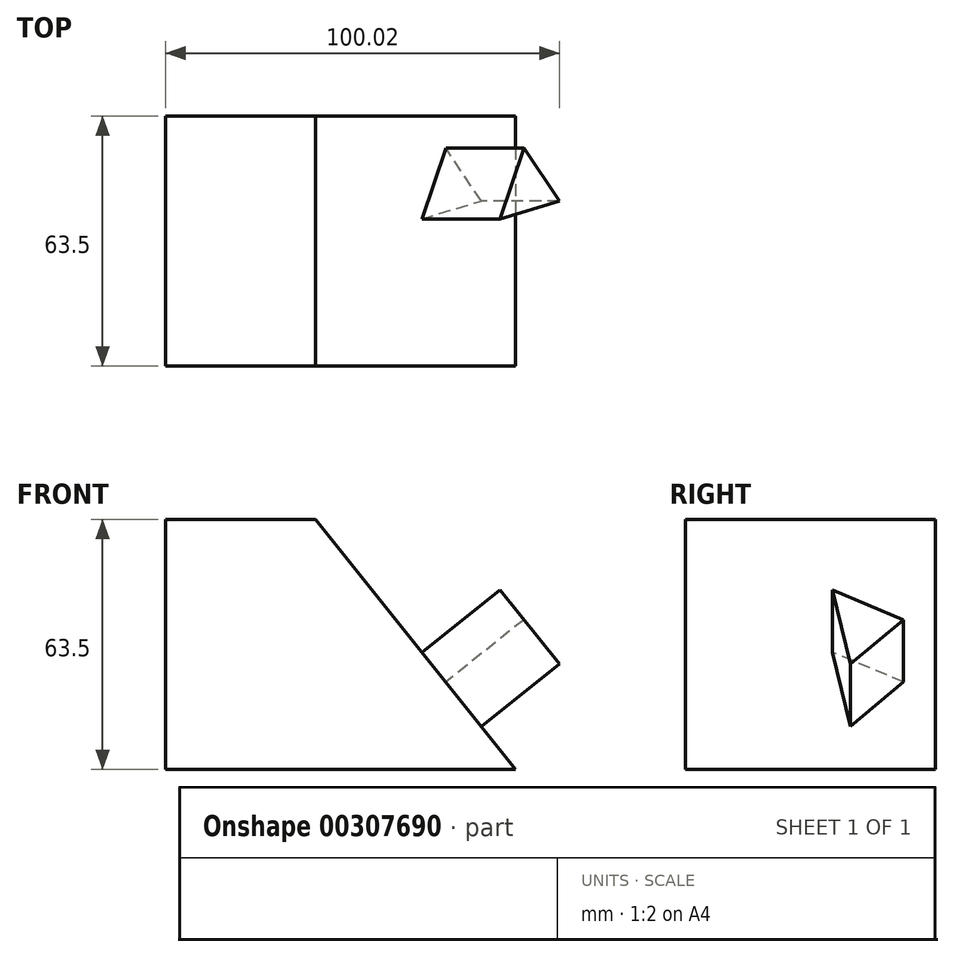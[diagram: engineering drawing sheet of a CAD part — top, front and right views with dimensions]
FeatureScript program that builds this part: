
annotation { "Feature Type Name" : "Feature", "Feature Type Description" : "" }
export const myFeature = defineFeature(function(context is Context, id is Id, definition is map)
    precondition{}
    {
        {
            var Q0;
            Q0=qCreatedBy(makeId("Front.planeOp"),FACE);
            var sketch = newSketch(context, id + "F0", { "sketchPlane" : qUnion([Q0])});
            skLineSegment(sketch, "E0", {"start": v(-63.1, -47.1) * mm, "end": v(25.8, -47.1) * mm});
            skLineSegment(sketch, "E1", {"start": v(-63.1, -47.1) * mm, "end": v(-63.1, 16.4) * mm});
            skLineSegment(sketch, "E2", {"start": v(-63.1, 16.4) * mm, "end": v(-25, 16.4) * mm});
            skLineSegment(sketch, "E3", {"start": v(-25, 16.4) * mm, "end": v(25.8, -47.1) * mm});
            skSolve(sketch);
        }
        {
            var Q0;
            Q0=makeQuery(id+"F0.imprint","IMPRINT",FACE,{"disambiguationData":[TD([[makeQuery(id+"F0.imprint","IMPRINT",EDGE,{"derivedFrom":sQuery(id+"F0.wireOp",EDGE,"E0")}),1.0]])]});
            extrude(context, id + "F1", {"entities" : qUnion([Q0]), "oppositeDirection" : true, "depth" : 63.5 * mm});
        }
        {
            var Q0;
            Q0=makeQuery(id+"F1.opExtrude","SWEPT_FACE",FACE,{"disambiguationData":[OSD([sQuery(id+"F0.wireOp",EDGE,"E3")])]});
            var sketch = newSketch(context, id + "F2", { "sketchPlane" : qUnion([Q0])});
            skLineSegment(sketch, "E4", {"start": v(37.37, -14.75) * mm, "end": v(41.93, -38.96) * mm});
            skLineSegment(sketch, "E5", {"start": v(41.93, -38.96) * mm, "end": v(55.4, -24.5) * mm});
            skLineSegment(sketch, "E6", {"start": v(55.4, -24.5) * mm, "end": v(37.37, -14.75) * mm});
            skSolve(sketch);
        }
        {
            var Q0;
            Q0=makeQuery(id+"F2.imprint","IMPRINT",FACE,{"disambiguationData":[TD([[makeQuery(id+"F2.imprint","IMPRINT",EDGE,{"derivedFrom":sQuery(id+"F2.wireOp",EDGE,"E4")}),1.0]])]});
            extrude(context, id + "F3", {"entities" : qUnion([Q0]), "operationType" : NewBodyOperationType.ADD, "depth" : 25.4 * mm});
        }
    });
